# Revit family: BE_50893.1_en_GB
name_source: partatom
category: Lighting Fixtures
units: mm (PartAtom-declared; Revit-internal decimal feet)

## family parameters
Cut with Voids When Loaded = Yes
Host = Face
Light Source = Yes
Part Type = Normal
Room Calculation Point = Yes
Round Connector Dimension = Use Diameter
Shared = No

## types (1)
- BEGA_50893.1_K3
    Ambient_temperature = 25 °C
    Apparent Load = 0 VA
    BEGA_dummy = No
    BEGA_internal = Yes
    BEGA_internal_off = Yes
    BEGA_internal_on = Yes
    BEGA_internal_structure = Yes
    Bega_IES = Yes
    CE_conformity = yes
    Color Filter = 16777215
    Colour_rendering_index = CRI > 90
    Colour_temperature = 3000 K
    Current = 0,7 A
    Custom_made_product = No
    Default Elevation = 0 mm  [stored 0 ft]
    Description = Recessed ceiling luminaire
    Description_custom_made_product = Here you can specify modifications of your custom-made product
    Dimming Lamp Color Temperature Shift = <None>
    Energy_efficiency_class = LED A++ - A
    Installation_housing = No
    Installation_in_thermal_insulation = not suitable
    LED_module_designation = LED-0832/930
    Lamp = LED 28.1 W
    Lamp_luminous_flux = 3735 lm
    Load_Classification = Lighting
    Logo = <None>
    Luminaire_luminous_flux = 2568 lm
    M_A = No
    M_G = No
    M_W = No
    Manufacturer = BEGA
    Material_11 = BEGA_glass_opal
    Material_22 = BEGA_finishes_aluminium_matt
    Material_34 = BEGA_finishes_velvet_white_matt
    Model = 50893.1K3
    Order_number = 50893.1K3
    Order_number_PSU_DALI_controllable = ---
    Photometric Web File = BE_50993-1K3.ies
    Power_supply_unit_DALI_controllable = No
    Power_supply_unit_dimmable_1_to_10V = No
    Product_data_sheet = https://cdn.bega.com
    Protection_class = IP 20
    Recessed_depth = 155 mm
    Recessed_opening = 380 mm
    Safety_class = III
    Service_life_criteria = L70B50 @ 25 °C = 200000 h
    Tilt Angle = 0,00°
    URL = https://www.bega.com
    Update = 2022-10-25T04:00:06
    Voltage = 0 V
    Weight = 2.1 kg

note: [stored X ft] marks values corroborated as IEEE doubles in the binary element streams (Revit-internal decimal feet)

## geometry (parser evidence)
native form markers: Sweep x2
no freeform markers — native parametric forms only
